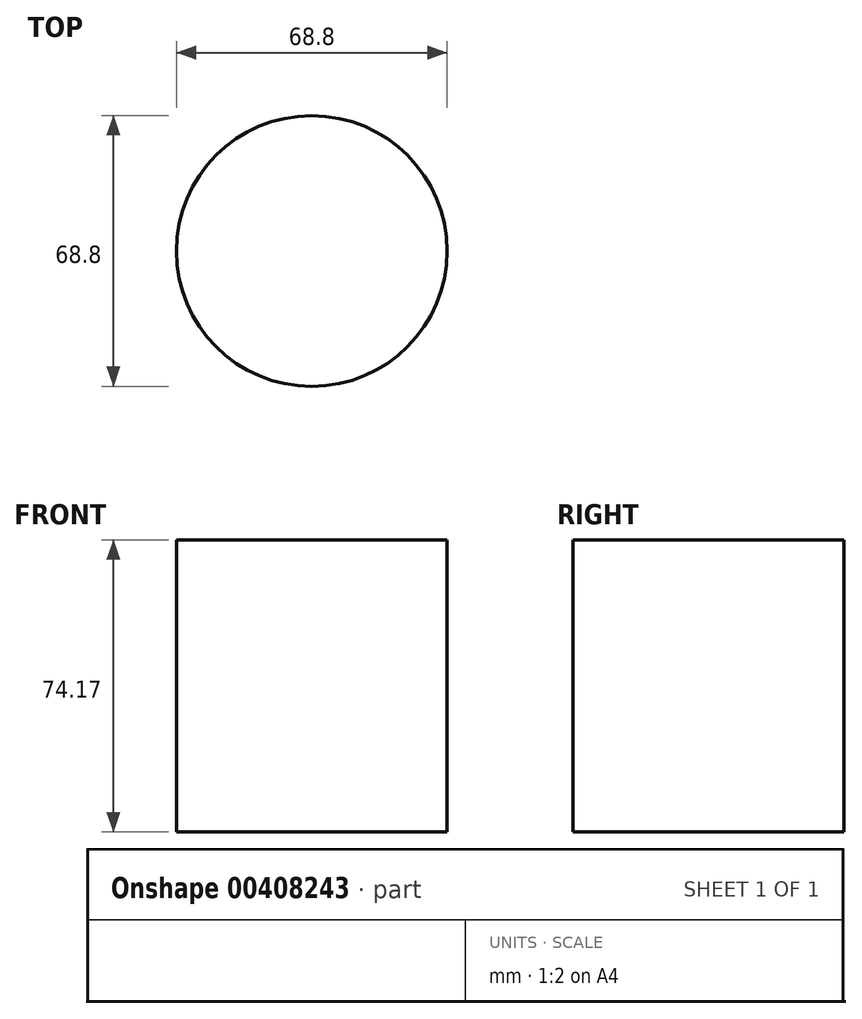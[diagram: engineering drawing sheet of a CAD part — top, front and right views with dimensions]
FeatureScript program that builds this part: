
annotation { "Feature Type Name" : "Feature", "Feature Type Description" : "" }
export const myFeature = defineFeature(function(context is Context, id is Id, definition is map)
    precondition{}
    {
        {
            var Q0;
            Q0=qCreatedBy(makeId("Top.planeOp"),FACE);
            var sketch = newSketch(context, id + "F0", { "sketchPlane" : qUnion([Q0])});
            skCircle(sketch, "E0", {"center": v(0, 0) * mm, "radius": 34.4 * mm});
            skSolve(sketch);
        }
        {
            var Q0;
            Q0=makeQuery(id+"F0.imprint","IMPRINT",FACE,{"disambiguationData":[TD([[makeQuery(id+"F0.imprint","IMPRINT",EDGE,{"derivedFrom":sQuery(id+"F0.wireOp",EDGE,"E0")}),1.0]])]});
            extrude(context, id + "F1", {"entities" : qUnion([Q0]), "depth" : 74.17 * mm});
        }
    });
